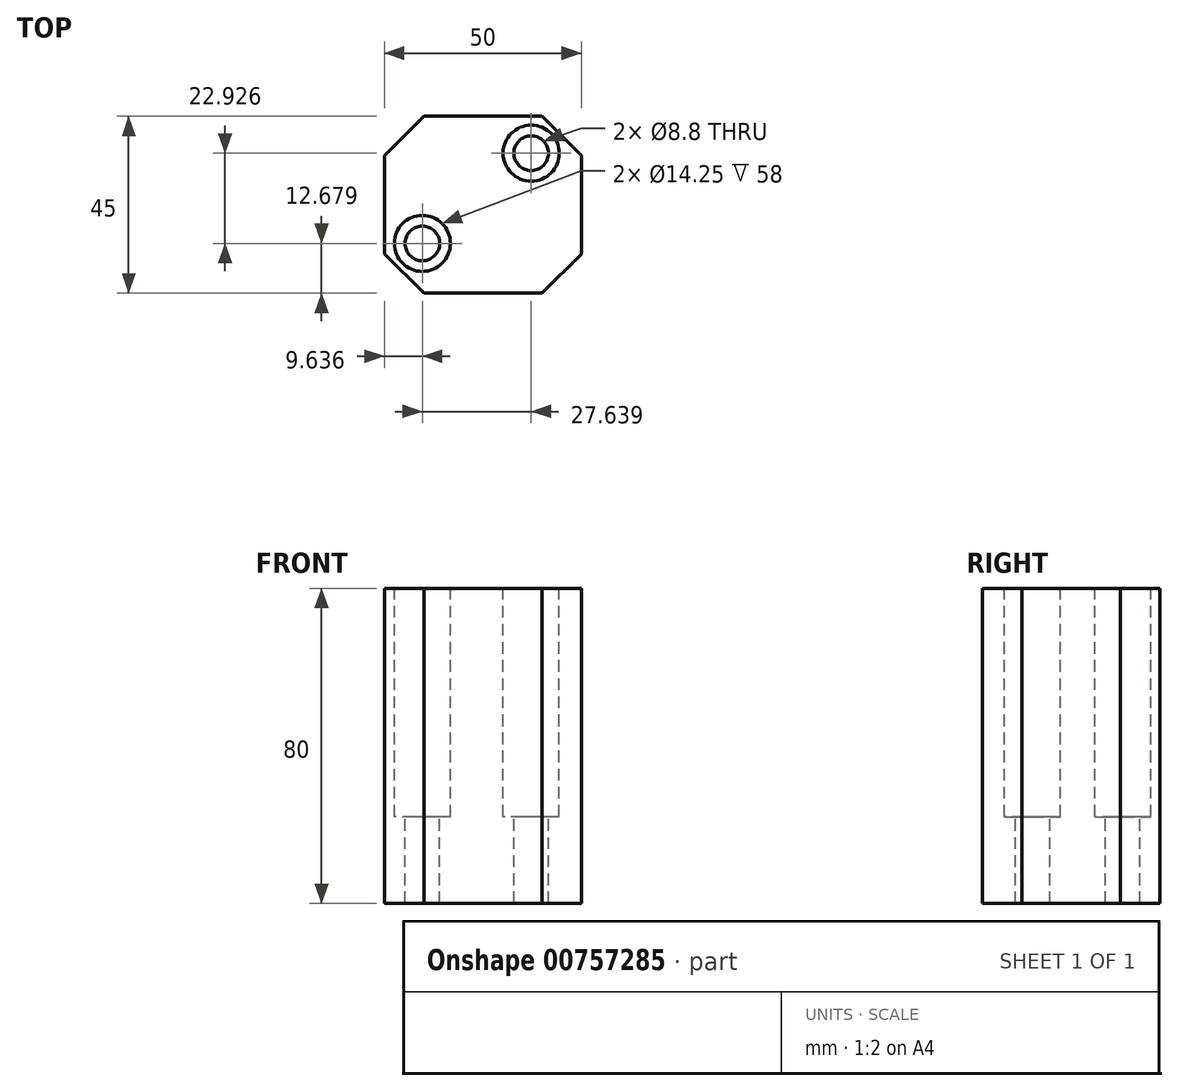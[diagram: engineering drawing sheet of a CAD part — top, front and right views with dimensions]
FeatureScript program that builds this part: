
annotation { "Feature Type Name" : "Feature", "Feature Type Description" : "" }
export const myFeature = defineFeature(function(context is Context, id is Id, definition is map)
    precondition{}
    {
        {
            var Q0;
            Q0=qCreatedBy(makeId("Top.planeOp"),FACE);
            var sketch = newSketch(context, id + "F0", { "sketchPlane" : qUnion([Q0])});
            skLineSegment(sketch, "E0.bottom", {"start": v(-27.27, 24.36) * mm, "end": v(22.73, 24.36) * mm});
            skLineSegment(sketch, "E0.top", {"start": v(-27.27, -20.64) * mm, "end": v(22.73, -20.64) * mm});
            skLineSegment(sketch, "E0.left", {"start": v(-27.27, 24.36) * mm, "end": v(-27.27, -20.64) * mm});
            skLineSegment(sketch, "E0.right", {"start": v(22.73, 24.36) * mm, "end": v(22.73, -20.64) * mm});
            skSolve(sketch);
        }
        {
            var Q0;
            Q0=makeQuery(id+"F0.imprint","IMPRINT",FACE,{"disambiguationData":[TD([[makeQuery(id+"F0.imprint","IMPRINT",EDGE,{"derivedFrom":sQuery(id+"F0.wireOp",EDGE,"E0.bottom")}),-1.0]])]});
            extrude(context, id + "F1", {"entities" : qUnion([Q0]), "depth" : 30 * mm, "offsetDistance" : 25 * mm});
        }
        {
            var Q0;
            Q0=makeQuery(id+"F1.opExtrude","SWEPT_EDGE",EDGE,{"disambiguationData":[OSD([sQuery(id+"F0.wireOp",EDGE,"E0.bottom"),sQuery(id+"F0.wireOp",EDGE,"E0.left")])]});
            var Q1;
            Q1=makeQuery(id+"F1.opExtrude","SWEPT_EDGE",EDGE,{"disambiguationData":[OSD([sQuery(id+"F0.wireOp",EDGE,"E0.top"),sQuery(id+"F0.wireOp",EDGE,"E0.right")])]});
            var Q2;
            Q2=makeQuery(id+"F1.opExtrude","SWEPT_EDGE",EDGE,{"disambiguationData":[OSD([sQuery(id+"F0.wireOp",EDGE,"E0.bottom"),sQuery(id+"F0.wireOp",EDGE,"E0.right")])]});
            var Q3;
            Q3=makeQuery(id+"F1.opExtrude","SWEPT_EDGE",EDGE,{"disambiguationData":[OSD([sQuery(id+"F0.wireOp",EDGE,"E0.top"),sQuery(id+"F0.wireOp",EDGE,"E0.left")])]});
            chamfer(context, id + "F2", {"entities" : qUnion([Q0, Q1, Q2, Q3]), "width" : 10 * mm, "tangentPropagation" : true});
        }
        {
            var Q0;
            Q0=makeQuery(id+"F1.opExtrude","CAP_FACE",FACE,{"disambiguationData":[OSD([sQuery(id+"F0.wireOp",EDGE,"E0.bottom"),sQuery(id+"F0.wireOp",EDGE,"E0.top"),sQuery(id+"F0.wireOp",EDGE,"E0.left"),sQuery(id+"F0.wireOp",EDGE,"E0.right")])],"isStart":false});
            var sketch = newSketch(context, id + "F3", { "sketchPlane" : qUnion([Q0])});
            skPoint(sketch, "E1", {"position": v(-17.63, -7.96) * mm});
            skPoint(sketch, "E2", {"position": v(10, 14.97) * mm});
            skSolve(sketch);
        }
        {
            var Q0;
            Q0=sQuery(id+"F3.wireOp",VERTEX,"E1");
            var Q1;
            Q1=sQuery(id+"F3.wireOp",VERTEX,"E2");
            var Q2;
            Q2=makeQuery(id+"F1.opExtrude","SWEPT_BODY",BODY,{"disambiguationData":[OSD([sQuery(id+"F0.wireOp",EDGE,"E0.bottom"),sQuery(id+"F0.wireOp",EDGE,"E0.top"),sQuery(id+"F0.wireOp",EDGE,"E0.left"),sQuery(id+"F0.wireOp",EDGE,"E0.right")])]});
            hole(context, id + "F4", {"style" : HoleStyle.C_BORE, "endStyle" : HoleEndStyle.THROUGH, "standardTappedOrClearance" : lookupTablePath({ "standard" : "ISO", "fit" : "Normal", "size" : "M8", "type" : "Clearance" }), "standardBlindInLast" : lookupTablePath({ "fit" : "Standard", "standard" : "ISO", "size" : "M8", "type" : "Clearance" }), "holeDiameter" : 8.8 * mm, "cBoreDiameter" : 14.25 * mm, "cBoreDepth" : 8 * mm, "majorDiameter" : 5 * mm, "isTappedThrough" : true, "tappedDepth" : 17.9 * mm, "tapClearance" : 3, "locations" : qUnion([Q0, Q1]), "scope" : qUnion([Q2])});
        }
        {
            var Q0;
            Q0=makeQuery(id+"F1.opExtrude","CAP_FACE",FACE,{"disambiguationData":[OSD([sQuery(id+"F0.wireOp",EDGE,"E0.bottom"),sQuery(id+"F0.wireOp",EDGE,"E0.top"),sQuery(id+"F0.wireOp",EDGE,"E0.left"),sQuery(id+"F0.wireOp",EDGE,"E0.right")])],"isStart":false});
            extrude(context, id + "F5", {"entities" : qUnion([Q0]), "operationType" : NewBodyOperationType.ADD, "depth" : 50 * mm, "offsetDistance" : 25 * mm});
        }
    });
